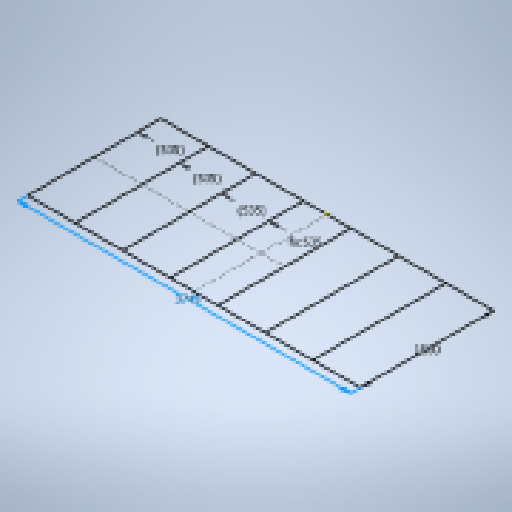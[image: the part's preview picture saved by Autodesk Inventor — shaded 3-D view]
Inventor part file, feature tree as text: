
AUTODESK INVENTOR PART (.ipt)
format: ipt  version: 2025 (Build 290162010, 162A)  size: 140,288 bytes
history: native  units: mm
features: sketch x1
ambient origin geometry x8: Origin, YZ Plane, XZ Plane, XY Plane, X Axis, Y Axis, Z Axis, Center Point
feature tree (1):
  sketch  "Sketch1"  dims[d0=3745.0mm d1=1500.0mm d5=2700.0mm d7=535.0mm d8=535.0mm d9=535.0mm d10=535.0mm]
